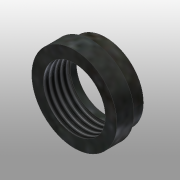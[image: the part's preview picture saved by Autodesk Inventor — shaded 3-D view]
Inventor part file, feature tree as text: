
AUTODESK INVENTOR PART (.ipt)
format: ipt  version: 2016 (Build 200138000, 138)  size: 122,880 bytes
history: native  units: mm
features: extrude x3, sketch x3, hole x1
ambient origin geometry x8: Origin, YZ Plane, XZ Plane, XY Plane, X Axis, Y Axis, Z Axis, Center Point
bodies: Solid1 (feature_tree)
feature tree (7):
  extrude  "Extrusion1"  Depth=3.0mm TaperAngle=0.0deg
  extrude  "Extrusion2"  Depth=2.5mm TaperAngle=0.0deg
  extrude  "Extrusion3"  Depth=2.5mm TaperAngle=0.0deg
  hole  "Hole1"  [1 undecoded]
  sketch  "Sketch1"  dims[d0=15.0mm d1=3.0mm d2=0.0mm]
  sketch  "Sketch2"  dims[d3=13.3mm d4=2.5mm d5=0.0mm]
  sketch  "Sketch3"  dims[d6=10.3mm d7=2.5mm d8=0.0mm d18=10.0mm d19=10.0mm d11=10.917mm d12=24.0mm d13=4.0mm d14=2.0mm d15=90.0deg d16=4.4mm d17=0.0mm]
note: 1 required parameter value undecoded (feature->parameter linkage not recoverable at this tier; creation-order binding heuristic only, values carry confidence <= 0.55)
